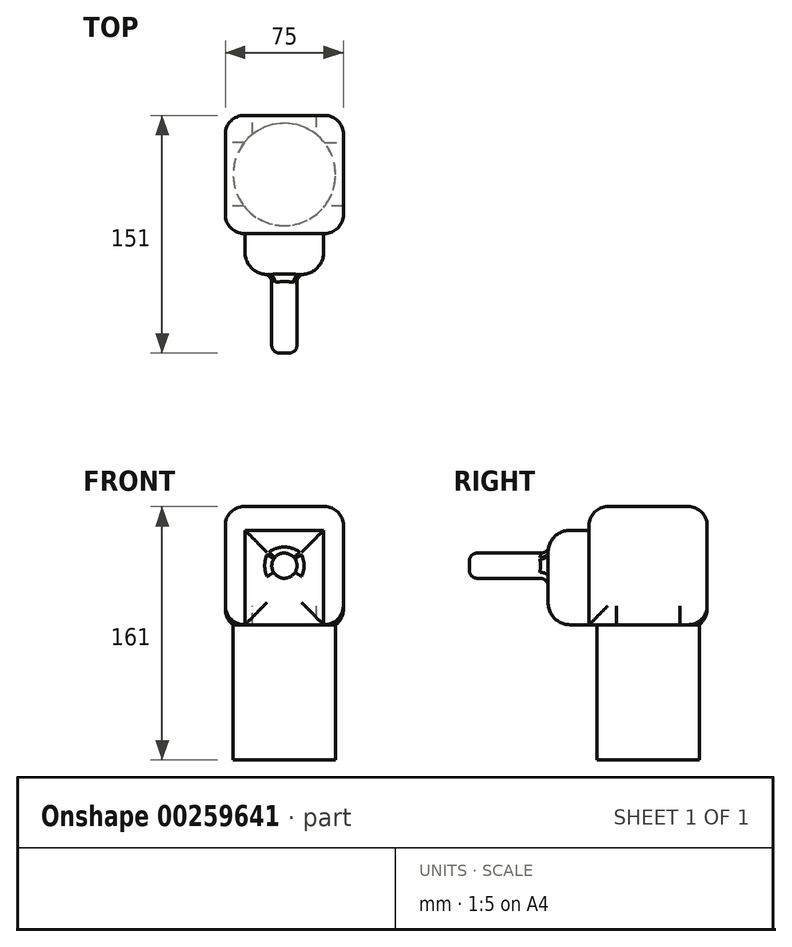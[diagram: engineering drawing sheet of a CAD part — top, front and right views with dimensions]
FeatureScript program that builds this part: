
annotation { "Feature Type Name" : "Feature", "Feature Type Description" : "" }
export const myFeature = defineFeature(function(context is Context, id is Id, definition is map)
    precondition{}
    {
        {
            var Q0;
            Q0=qCreatedBy(makeId("Top.planeOp"),FACE);
            var sketch = newSketch(context, id + "F0", { "sketchPlane" : qUnion([Q0])});
            skCircle(sketch, "E0", {"center": v(0, 0) * mm, "radius": 32.5 * mm});
            skSolve(sketch);
        }
        {
            var Q0;
            Q0 = qSketchRegion(id + "F0", true);
            extrude(context, id + "F1", {"entities" : qUnion([Q0]), "oppositeDirection" : true, "depth" : 86 * mm});
        }
        {
            var Q0;
            Q0=makeQuery(id+"F1.opExtrude","CAP_FACE",FACE,{"disambiguationData":[OSD([sQuery(id+"F0.wireOp",EDGE,"E0")])],"isStart":true});
            var sketch = newSketch(context, id + "F2", { "sketchPlane" : qUnion([Q0])});
            skLineSegment(sketch, "E1.bottom", {"start": v(37.5, 37.5) * mm, "end": v(-37.5, 37.5) * mm});
            skLineSegment(sketch, "E1.top", {"start": v(37.5, -37.5) * mm, "end": v(-37.5, -37.5) * mm});
            skLineSegment(sketch, "E1.left", {"start": v(37.5, 37.5) * mm, "end": v(37.5, -37.5) * mm});
            skLineSegment(sketch, "E1.right", {"start": v(-37.5, 37.5) * mm, "end": v(-37.5, -37.5) * mm});
            skPoint(sketch, "E1.middle", {"position": v(0, 0) * mm});
            skSolve(sketch);
        }
        {
            var Q0;
            Q0 = qSketchRegion(id + "F2", true);
            extrude(context, id + "F3", {"entities" : qUnion([Q0]), "operationType" : NewBodyOperationType.ADD, "depth" : 75 * mm});
        }
        {
            var Q0;
            Q0=makeQuery(id+"F3.opExtrude","SWEPT_FACE",FACE,{"disambiguationData":[OSD([sQuery(id+"F2.wireOp",EDGE,"E1.top")])]});
            var sketch = newSketch(context, id + "F4", { "sketchPlane" : qUnion([Q0])});
            skLineSegment(sketch, "E2", {"start": v(0, 75) * mm, "end": v(0, 0) * mm, "construction": true});
            skLineSegment(sketch, "E3.bottom", {"start": v(-25, 0) * mm, "end": v(25, 0) * mm});
            skLineSegment(sketch, "E3.top", {"start": v(-25, 60) * mm, "end": v(25, 60) * mm});
            skLineSegment(sketch, "E3.left", {"start": v(-25, 0) * mm, "end": v(-25, 60) * mm});
            skLineSegment(sketch, "E3.right", {"start": v(25, 0) * mm, "end": v(25, 60) * mm});
            skSolve(sketch);
        }
        {
            var Q0;
            Q0 = qSketchRegion(id + "F4", true);
            extrude(context, id + "F5", {"entities" : qUnion([Q0]), "operationType" : NewBodyOperationType.ADD, "depth" : 26 * mm});
        }
        {
            var Q0;
            Q0=makeQuery(id+"F5.opExtrude","CAP_FACE",FACE,{"disambiguationData":[OSD([sQuery(id+"F4.wireOp",EDGE,"E3.bottom"),sQuery(id+"F4.wireOp",EDGE,"E3.top"),sQuery(id+"F4.wireOp",EDGE,"E3.left"),sQuery(id+"F4.wireOp",EDGE,"E3.right")])],"isStart":false});
            var sketch = newSketch(context, id + "F6", { "sketchPlane" : qUnion([Q0])});
            skLineSegment(sketch, "E4.0", {"start": v(-37.5, 75) * mm, "end": v(-37.5, 0) * mm, "construction": true});
            skLineSegment(sketch, "E5.0", {"start": v(37.5, 75) * mm, "end": v(37.5, 0) * mm, "construction": true});
            skLineSegment(sketch, "E6.0", {"start": v(37.5, 75) * mm, "end": v(-37.5, 75) * mm, "construction": true});
            skLineSegment(sketch, "E7", {"start": v(-37.5, 37.5) * mm, "end": v(37.5, 37.5) * mm, "construction": true});
            skCircle(sketch, "E8", {"center": v(0, 37.5) * mm, "radius": 8 * mm});
            skSolve(sketch);
        }
        {
            var Q0;
            Q0 = qSketchRegion(id + "F6", true);
            extrude(context, id + "F7", {"entities" : qUnion([Q0]), "operationType" : NewBodyOperationType.ADD, "depth" : 50 * mm});
        }
        {
            var Q0;
            Q0=makeQuery(id+"F3.opExtrude","SWEPT_FACE",FACE,{"disambiguationData":[OSD([sQuery(id+"F2.wireOp",EDGE,"E1.left")])]});
            var Q1;
            Q1=makeQuery(id+"F3.opExtrude","SWEPT_FACE",FACE,{"disambiguationData":[OSD([sQuery(id+"F2.wireOp",EDGE,"E1.bottom")])]});
            var Q2;
            Q2=makeQuery(id+"F3.opExtrude","CAP_FACE",FACE,{"disambiguationData":[OSD([sQuery(id+"F2.wireOp",EDGE,"E1.bottom"),sQuery(id+"F2.wireOp",EDGE,"E1.top"),sQuery(id+"F2.wireOp",EDGE,"E1.left"),sQuery(id+"F2.wireOp",EDGE,"E1.right")])],"isStart":false});
            var Q3;
            Q3=makeQuery(id+"F3.opExtrude","SWEPT_FACE",FACE,{"disambiguationData":[OSD([sQuery(id+"F2.wireOp",EDGE,"E1.right")])]});
            fillet(context, id + "F8", {"entities" : qUnion([Q0, Q1, Q2, Q3]), "radius" : 12 * mm, "tangentPropagation" : true, "allowEdgeOverflow" : false});
        }
        {
            var Q0;
            Q0=makeQuery(id+"F5.opExtrude","CAP_EDGE",EDGE,{"disambiguationData":[OSD([sQuery(id+"F4.wireOp",EDGE,"E3.right")])],"isStart":false});
            var Q1;
            Q1=makeQuery(id+"F5.opExtrude","CAP_EDGE",EDGE,{"disambiguationData":[OSD([sQuery(id+"F4.wireOp",EDGE,"E3.top")])],"isStart":false});
            var Q2;
            {var subQ0=sQuery(id+"F2.wireOp",EDGE,"E1.top");Q2=makeQuery(id+"F8.opFillet","BLEND_EDGE",EDGE,{"blendedFrom":[makeQuery(id+"F3.opExtrude","SWEPT_EDGE",EDGE,{"disambiguationData":[OSD([subQ0,sQuery(id+"F2.wireOp",EDGE,"E1.left")])]}),makeQuery(id+"F3.opExtrude","SWEPT_FACE",FACE,{"disambiguationData":[OSD([subQ0])]})],"blendedInto":[makeQuery(id+"F3.opExtrude","SWEPT_FACE",FACE,{"disambiguationData":[OSD([subQ0])]})]});}
            var Q3;
            Q3=makeQuery(id+"F5.opExtrude","CAP_EDGE",EDGE,{"disambiguationData":[OSD([sQuery(id+"F4.wireOp",EDGE,"E3.top")])],"isStart":true});
            var Q4;
            Q4=makeQuery(id+"F5.opExtrude","CAP_EDGE",EDGE,{"disambiguationData":[OSD([sQuery(id+"F4.wireOp",EDGE,"E3.right")])],"isStart":true});
            var Q5;
            Q5=makeQuery(id+"F5.opExtrude","CAP_EDGE",EDGE,{"disambiguationData":[OSD([sQuery(id+"F4.wireOp",EDGE,"E3.left")])],"isStart":true});
            var Q6;
            Q6=makeQuery(id+"F5.opExtrude","CAP_EDGE",EDGE,{"disambiguationData":[OSD([sQuery(id+"F4.wireOp",EDGE,"E3.left")])],"isStart":false});
            var Q7;
            Q7=makeQuery(id+"F5.opExtrude","CAP_EDGE",EDGE,{"disambiguationData":[OSD([sQuery(id+"F4.wireOp",EDGE,"E3.bottom")])],"isStart":false});
            fillet(context, id + "F9", {"entities" : qUnion([Q0, Q1, Q2, Q3, Q4, Q5, Q6, Q7]), "radius" : 14 * mm, "tangentPropagation" : true, "allowEdgeOverflow" : false});
        }
        {
            var Q0;
            Q0=makeQuery(id+"F7.opExtrude","SWEPT_FACE",FACE,{"disambiguationData":[OSD([sQuery(id+"F6.wireOp",EDGE,"E8")])]});
            fillet(context, id + "F10", {"entities" : qUnion([Q0]), "radius" : 5 * mm, "tangentPropagation" : true, "allowEdgeOverflow" : false});
        }
    });
